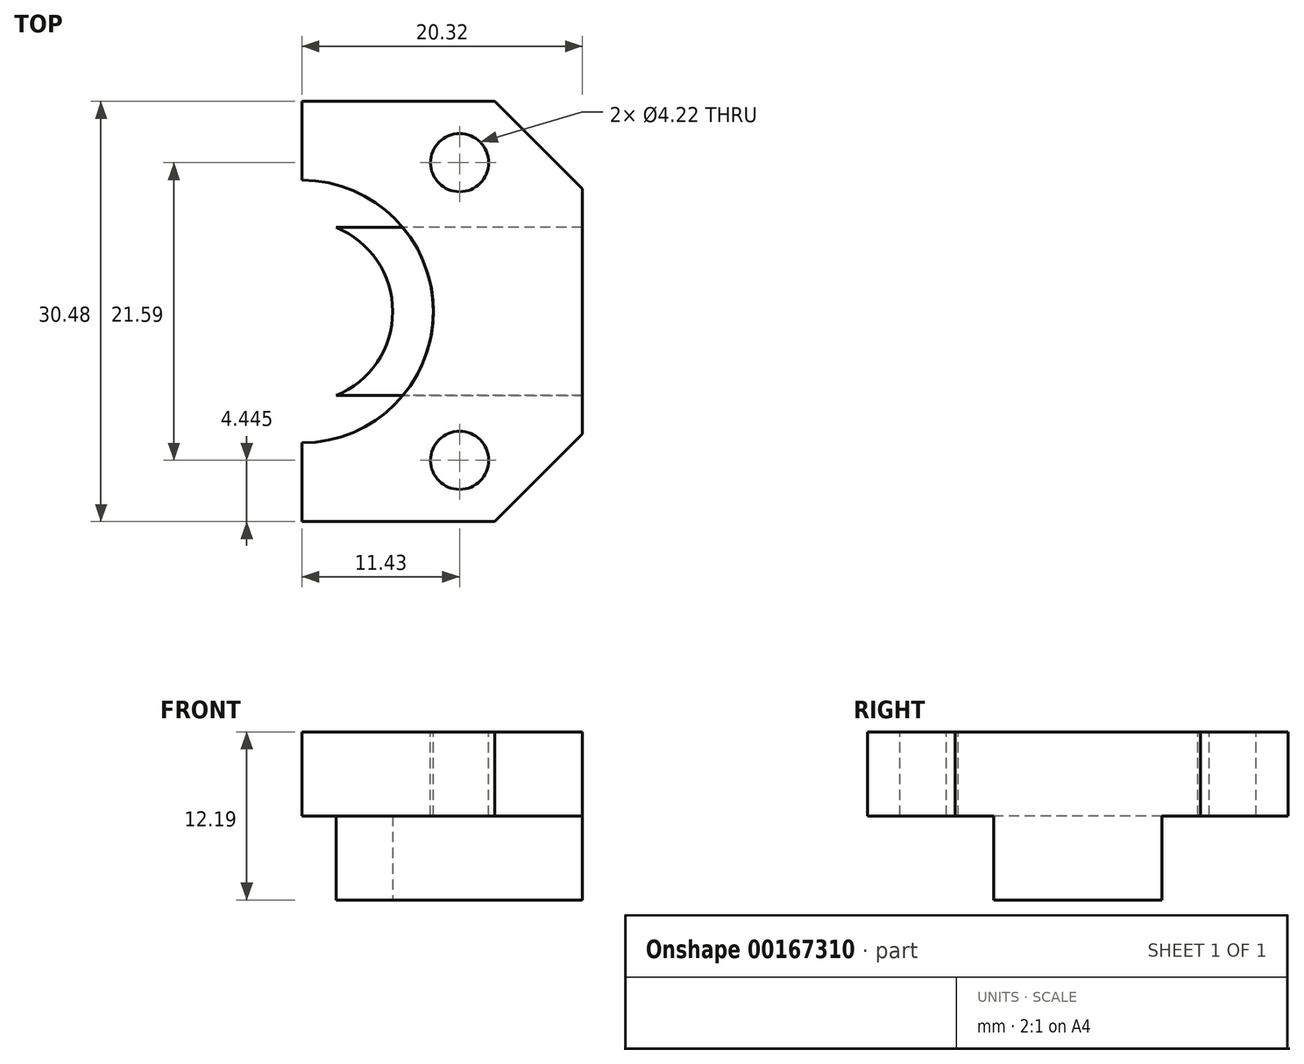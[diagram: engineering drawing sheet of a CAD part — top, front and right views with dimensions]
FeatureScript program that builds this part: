
annotation { "Feature Type Name" : "Feature", "Feature Type Description" : "" }
export const myFeature = defineFeature(function(context is Context, id is Id, definition is map)
    precondition{}
    {
        {
            var Q0;
            Q0=qCreatedBy(makeId("Top.planeOp"),FACE);
            var sketch = newSketch(context, id + "F0", { "sketchPlane" : qUnion([Q0])});
            skArc(sketch, "E0", {"start": v(0, -6.58) * mm, "mid": v(6.58, 0) * mm, "end": v(0, 6.58) * mm});
            skLineSegment(sketch, "E1", {"start": v(20.32, -8.89) * mm, "end": v(20.32, 8.9) * mm});
            skLineSegment(sketch, "E2", {"start": v(13.97, 15.24) * mm, "end": v(0, 15.24) * mm});
            skLineSegment(sketch, "E3", {"start": v(0, 15.24) * mm, "end": v(0, 6.58) * mm});
            skLineSegment(sketch, "E4", {"start": v(13.97, -15.24) * mm, "end": v(0, -15.24) * mm});
            skLineSegment(sketch, "E5", {"start": v(0, -6.58) * mm, "end": v(0, -15.24) * mm});
            skPoint(sketch, "E6.orphan", {"position": v(6.58, 0) * mm});
            skPoint(sketch, "E7.orphan", {"position": v(0, -6.3) * mm});
            skPoint(sketch, "E8.visualSharp", {"position": v(20.32, -15.24) * mm});
            skPoint(sketch, "E9.visualSharp", {"position": v(20.32, 15.24) * mm});
            skLineSegment(sketch, "E10", {"start": v(13.97, 15.24) * mm, "end": v(20.32, 8.9) * mm});
            skLineSegment(sketch, "E11", {"start": v(20.32, -8.89) * mm, "end": v(13.97, -15.24) * mm});
            skSolve(sketch);
        }
        {
            var Q0;
            Q0 = qSketchRegion(id + "F0", true);
            extrude(context, id + "F1", {"entities" : qUnion([Q0]), "depth" : 12.2 * mm});
        }
        {
            var Q0;
            Q0=makeQuery(id+"F1.opExtrude","SWEPT_FACE",FACE,{"disambiguationData":[OSD([sQuery(id+"F0.wireOp",EDGE,"E3")])]});
            var sketch = newSketch(context, id + "F2", { "sketchPlane" : qUnion([Q0])});
            skLineSegment(sketch, "E12", {"start": v(-15.24, 6.1) * mm, "end": v(-6.1, 6.1) * mm});
            skLineSegment(sketch, "E13", {"start": v(-6.1, 6.1) * mm, "end": v(-6.1, -2.73) * mm});
            skLineSegment(sketch, "E14", {"start": v(-6.1, -2.73) * mm, "end": v(6.1, -2.73) * mm});
            skLineSegment(sketch, "E15", {"start": v(6.1, -2.73) * mm, "end": v(6.1, 6.1) * mm});
            skLineSegment(sketch, "E16", {"start": v(6.1, 6.1) * mm, "end": v(15.24, 6.1) * mm});
            skLineSegment(sketch, "E17", {"start": v(15.24, 6.1) * mm, "end": v(15.24, -9.26) * mm});
            skLineSegment(sketch, "E18", {"start": v(15.24, -9.26) * mm, "end": v(-15.24, -9.26) * mm});
            skLineSegment(sketch, "E19", {"start": v(-15.24, -9.26) * mm, "end": v(-15.24, 6.1) * mm});
            skPoint(sketch, "E20.orphan", {"position": v(-6.58, 6.1) * mm});
            skSolve(sketch);
        }
        {
            var Q0;
            Q0 = qSketchRegion(id + "F2", true);
            extrude(context, id + "F3", {"entities" : qUnion([Q0]), "operationType" : NewBodyOperationType.REMOVE, "endBound" : BoundingType.THROUGH_ALL, "oppositeDirection" : true, "depth" : 25.4 * mm});
        }
        {
            var Q0;
            Q0=makeQuery(id+"F1.opExtrude","CAP_FACE",FACE,{"disambiguationData":[OSD([sQuery(id+"F0.wireOp",EDGE,"E0"),sQuery(id+"F0.wireOp",EDGE,"E1"),sQuery(id+"F0.wireOp",EDGE,"E2"),sQuery(id+"F0.wireOp",EDGE,"E3"),sQuery(id+"F0.wireOp",EDGE,"E4"),sQuery(id+"F0.wireOp",EDGE,"E5"),sQuery(id+"F0.wireOp",EDGE,"E8.filletArc"),sQuery(id+"F0.wireOp",EDGE,"E9.filletArc")])],"isStart":false});
            var sketch = newSketch(context, id + "F4", { "sketchPlane" : qUnion([Q0])});
            skCircle(sketch, "E21", {"center": v(0, 0) * mm, "radius": 9.53 * mm});
            skSolve(sketch);
        }
        {
            var Q0;
            Q0 = qSketchRegion(id + "F4", true);
            var Q1;
            Q1=makeQuery(id+"F3.boolean.opBoolean","COPY",FACE,{"derivedFrom":makeQuery(id+"F3.opExtrude","SWEPT_FACE",FACE,{"disambiguationData":[OSD([sQuery(id+"F2.wireOp",EDGE,"E12")])]})});
            extrude(context, id + "F5", {"entities" : qUnion([Q0]), "operationType" : NewBodyOperationType.REMOVE, "endBound" : BoundingType.UP_TO_SURFACE, "oppositeDirection" : true, "endBoundEntityFace" : qUnion([Q1]), "depth" : 2.54 * mm});
        }
        {
            var Q0;
            Q0=makeQuery(id+"F1.opExtrude","CAP_FACE",FACE,{"disambiguationData":[OSD([sQuery(id+"F0.wireOp",EDGE,"E0"),sQuery(id+"F0.wireOp",EDGE,"E1"),sQuery(id+"F0.wireOp",EDGE,"E2"),sQuery(id+"F0.wireOp",EDGE,"E3"),sQuery(id+"F0.wireOp",EDGE,"E4"),sQuery(id+"F0.wireOp",EDGE,"E5"),sQuery(id+"F0.wireOp",EDGE,"E10"),sQuery(id+"F0.wireOp",EDGE,"E11")])],"isStart":false});
            var sketch = newSketch(context, id + "F6", { "sketchPlane" : qUnion([Q0])});
            skLineSegment(sketch, "E22", {"start": v(11.43, 10.8) * mm, "end": v(11.43, -10.8) * mm});
            skSolve(sketch);
        }
        {
            var Q0;
            Q0=sQuery(id+"F6.wireOp",VERTEX,"E22.start");
            var Q1;
            Q1=sQuery(id+"F6.wireOp",VERTEX,"E22.end");
            var Q2;
            Q2=makeQuery(id+"F1.opExtrude","SWEPT_BODY",BODY,{"disambiguationData":[OSD([sQuery(id+"F0.wireOp",EDGE,"E0"),sQuery(id+"F0.wireOp",EDGE,"E1"),sQuery(id+"F0.wireOp",EDGE,"E2"),sQuery(id+"F0.wireOp",EDGE,"E3"),sQuery(id+"F0.wireOp",EDGE,"E4"),sQuery(id+"F0.wireOp",EDGE,"E5"),sQuery(id+"F0.wireOp",EDGE,"E10"),sQuery(id+"F0.wireOp",EDGE,"E11")])]});
            hole(context, id + "F7", {"style" : HoleStyle.SIMPLE, "endStyle" : HoleEndStyle.THROUGH, "holeDiameter" : 4.22 * mm, "locations" : qUnion([Q0, Q1]), "scope" : qUnion([Q2]), "isTappedThrough" : true});
        }
    });
